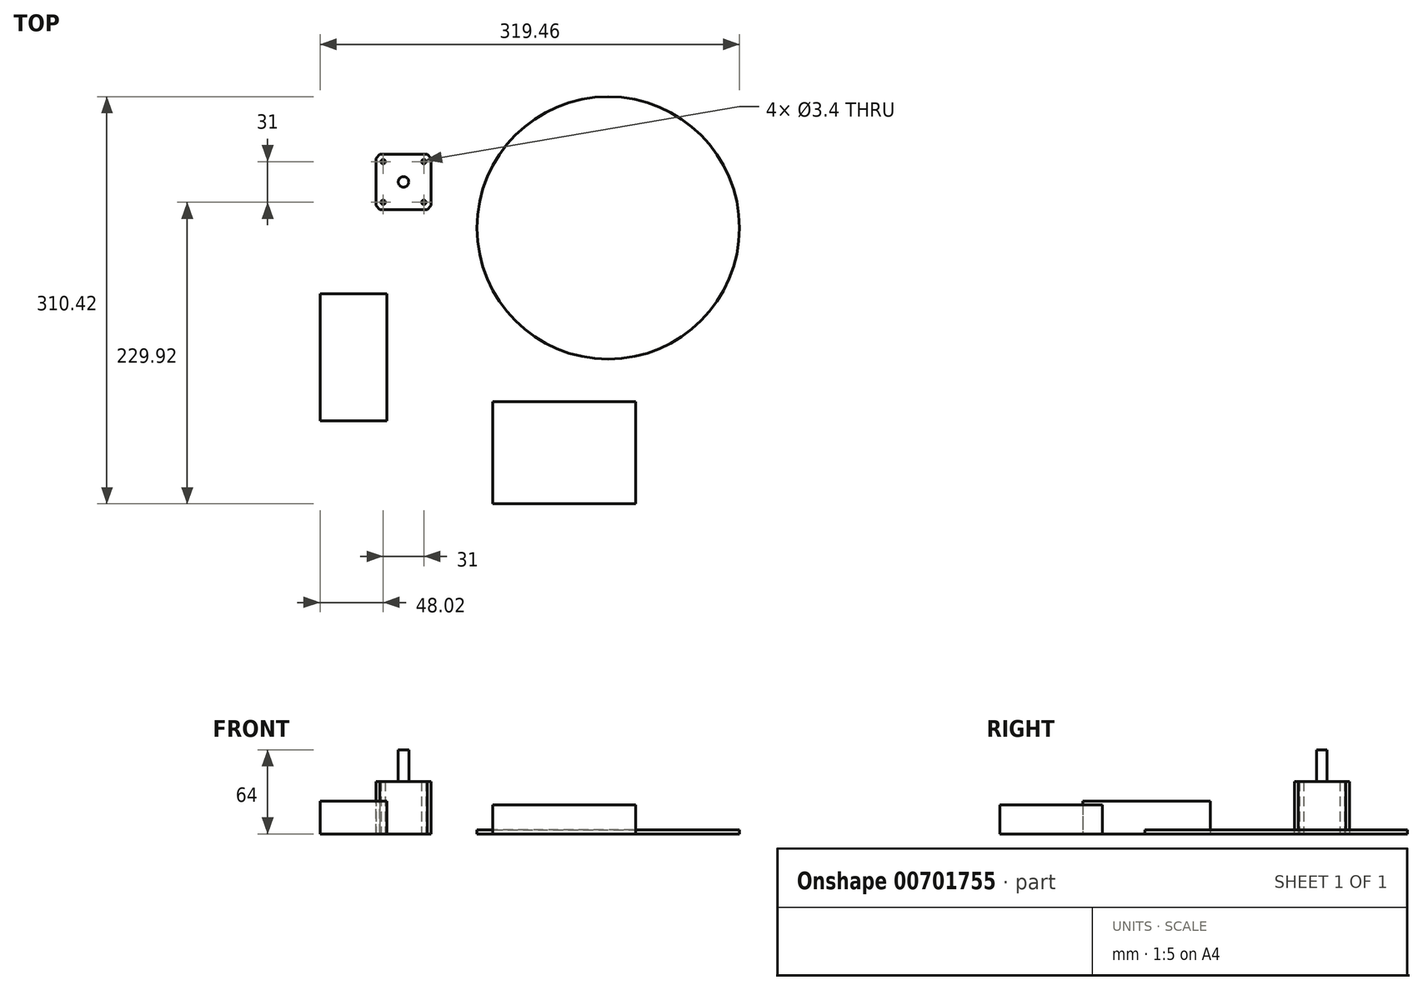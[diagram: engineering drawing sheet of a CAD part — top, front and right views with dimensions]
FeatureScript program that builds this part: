
annotation { "Feature Type Name" : "Feature", "Feature Type Description" : "" }
export const myFeature = defineFeature(function(context is Context, id is Id, definition is map)
    precondition{}
    {
        {
            var Q0;
            Q0=qCreatedBy(makeId("Top.planeOp"),FACE);
            var sketch = newSketch(context, id + "F0", { "sketchPlane" : qUnion([Q0])});
            skLineSegment(sketch, "E0.bottom", {"start": v(-42, 42) * mm, "end": v(0, 42) * mm});
            skLineSegment(sketch, "E0.top", {"start": v(-42, 0) * mm, "end": v(0, 0) * mm});
            skLineSegment(sketch, "E0.left", {"start": v(-42, 42) * mm, "end": v(-42, 0) * mm});
            skLineSegment(sketch, "E0.right", {"start": v(0, 42) * mm, "end": v(0, 0) * mm});
            skCircle(sketch, "E1", {"center": v(-36.5, 36.5) * mm, "radius": 1.7 * mm});
            skCircle(sketch, "E2.0.1.0", {"center": v(-36.5, 5.5) * mm, "radius": 1.7 * mm});
            skCircle(sketch, "E2.1.0.0", {"center": v(-5.5, 36.5) * mm, "radius": 1.7 * mm});
            skCircle(sketch, "E2.1.1.0", {"center": v(-5.5, 5.5) * mm, "radius": 1.7 * mm});
            skLineSegment(sketch, "E2.direction1", {"start": v(-36.5, 36.5) * mm, "end": v(-5.5, 36.5) * mm, "construction": true});
            skLineSegment(sketch, "E2.direction2", {"start": v(-36.5, 36.5) * mm, "end": v(-36.5, 5.5) * mm, "construction": true});
            skSolve(sketch);
        }
        {
            var Q0;
            Q0=makeQuery(id+"F0.imprint","IMPRINT",FACE,{"disambiguationData":[TD([[makeQuery(id+"F0.imprint","IMPRINT",EDGE,{"derivedFrom":sQuery(id+"F0.wireOp",EDGE,"E0.bottom")}),-1.0]])]});
            extrude(context, id + "F1", {"entities" : qUnion([Q0]), "depth" : 40 * mm, "offsetDistance" : 25 * mm});
        }
        {
            var Q0;
            Q0=makeQuery(id+"F1.opExtrude","CAP_FACE",FACE,{"disambiguationData":[OSD([sQuery(id+"F0.wireOp",EDGE,"E0.bottom"),sQuery(id+"F0.wireOp",EDGE,"E0.top"),sQuery(id+"F0.wireOp",EDGE,"E0.left"),sQuery(id+"F0.wireOp",EDGE,"E0.right")])],"isStart":false});
            var sketch = newSketch(context, id + "F2", { "sketchPlane" : qUnion([Q0])});
            skCircle(sketch, "E3", {"center": v(-21, 21) * mm, "radius": 4 * mm});
            skPoint(sketch, "E3.centerSnap0", {"position": v(-21, 42) * mm});
            skSolve(sketch);
        }
        {
            var Q0;
            Q0=makeQuery(id+"F2.imprint","IMPRINT",FACE,{"disambiguationData":[TD([[makeQuery(id+"F2.imprint","IMPRINT",EDGE,{"derivedFrom":sQuery(id+"F2.wireOp",EDGE,"E3")}),1.0]])]});
            extrude(context, id + "F3", {"entities" : qUnion([Q0]), "operationType" : NewBodyOperationType.ADD, "depth" : 24 * mm, "offsetDistance" : 25 * mm});
        }
        {
            var Q0;
            Q0=makeQuery(id+"F1.opExtrude","SWEPT_EDGE",EDGE,{"disambiguationData":[OSD([sQuery(id+"F0.wireOp",EDGE,"E0.bottom"),sQuery(id+"F0.wireOp",EDGE,"E0.right")])]});
            var Q1;
            Q1=makeQuery(id+"F1.opExtrude","SWEPT_EDGE",EDGE,{"disambiguationData":[OSD([sQuery(id+"F0.wireOp",EDGE,"E0.top"),sQuery(id+"F0.wireOp",EDGE,"E0.right")])]});
            var Q2;
            Q2=makeQuery(id+"F1.opExtrude","SWEPT_EDGE",EDGE,{"disambiguationData":[OSD([sQuery(id+"F0.wireOp",EDGE,"E0.top"),sQuery(id+"F0.wireOp",EDGE,"E0.left")])]});
            var Q3;
            Q3=makeQuery(id+"F1.opExtrude","SWEPT_EDGE",EDGE,{"disambiguationData":[OSD([sQuery(id+"F0.wireOp",EDGE,"E0.bottom"),sQuery(id+"F0.wireOp",EDGE,"E0.left")])]});
            chamfer(context, id + "F4", {"entities" : qUnion([Q0, Q1, Q2, Q3]), "width" : 3 * mm, "tangentPropagation" : true});
        }
        {
            var Q0;
            Q0=qCreatedBy(makeId("Top.planeOp"),FACE);
            var sketch = newSketch(context, id + "F5", { "sketchPlane" : qUnion([Q0])});
            skCircle(sketch, "E4", {"center": v(134.94, -14) * mm, "radius": 100 * mm});
            skSolve(sketch);
        }
        {
            var Q0;
            Q0=makeQuery(id+"F5.imprint","IMPRINT",FACE,{"disambiguationData":[TD([[makeQuery(id+"F5.imprint","IMPRINT",EDGE,{"derivedFrom":sQuery(id+"F5.wireOp",EDGE,"E4")}),1.0]])]});
            extrude(context, id + "F6", {"entities" : qUnion([Q0]), "depth" : 3 * mm, "offsetDistance" : 25 * mm});
        }
        {
            var Q0;
            Q0=qCreatedBy(makeId("Top.planeOp"),FACE);
            var sketch = newSketch(context, id + "F7", { "sketchPlane" : qUnion([Q0])});
            skLineSegment(sketch, "E5.bottom", {"start": v(-84.52, -64.1) * mm, "end": v(-33.52, -64.1) * mm});
            skLineSegment(sketch, "E5.top", {"start": v(-84.52, -161.1) * mm, "end": v(-33.52, -161.1) * mm});
            skLineSegment(sketch, "E5.left", {"start": v(-84.52, -64.1) * mm, "end": v(-84.52, -161.1) * mm});
            skLineSegment(sketch, "E5.right", {"start": v(-33.52, -64.1) * mm, "end": v(-33.52, -161.1) * mm});
            skSolve(sketch);
        }
        {
            var Q0;
            Q0=makeQuery(id+"F7.imprint","IMPRINT",FACE,{"disambiguationData":[TD([[makeQuery(id+"F7.imprint","IMPRINT",EDGE,{"derivedFrom":sQuery(id+"F7.wireOp",EDGE,"E5.bottom")}),-1.0]])]});
            extrude(context, id + "F8", {"entities" : qUnion([Q0]), "depth" : 25 * mm, "offsetDistance" : 25 * mm});
        }
        {
            var Q0;
            Q0=qCreatedBy(makeId("Top.planeOp"),FACE);
            var sketch = newSketch(context, id + "F9", { "sketchPlane" : qUnion([Q0])});
            skLineSegment(sketch, "E6.bottom", {"start": v(47.02, -146.42) * mm, "end": v(156.02, -146.42) * mm});
            skLineSegment(sketch, "E6.top", {"start": v(47.02, -224.42) * mm, "end": v(156.02, -224.42) * mm});
            skLineSegment(sketch, "E6.left", {"start": v(47.02, -146.42) * mm, "end": v(47.02, -224.42) * mm});
            skLineSegment(sketch, "E6.right", {"start": v(156.02, -146.42) * mm, "end": v(156.02, -224.42) * mm});
            skSolve(sketch);
        }
        {
            var Q0;
            Q0=makeQuery(id+"F9.imprint","IMPRINT",FACE,{"disambiguationData":[TD([[makeQuery(id+"F9.imprint","IMPRINT",EDGE,{"derivedFrom":sQuery(id+"F9.wireOp",EDGE,"E6.bottom")}),-1.0]])]});
            extrude(context, id + "F10", {"entities" : qUnion([Q0]), "depth" : 22 * mm, "offsetDistance" : 25 * mm});
        }
    });
